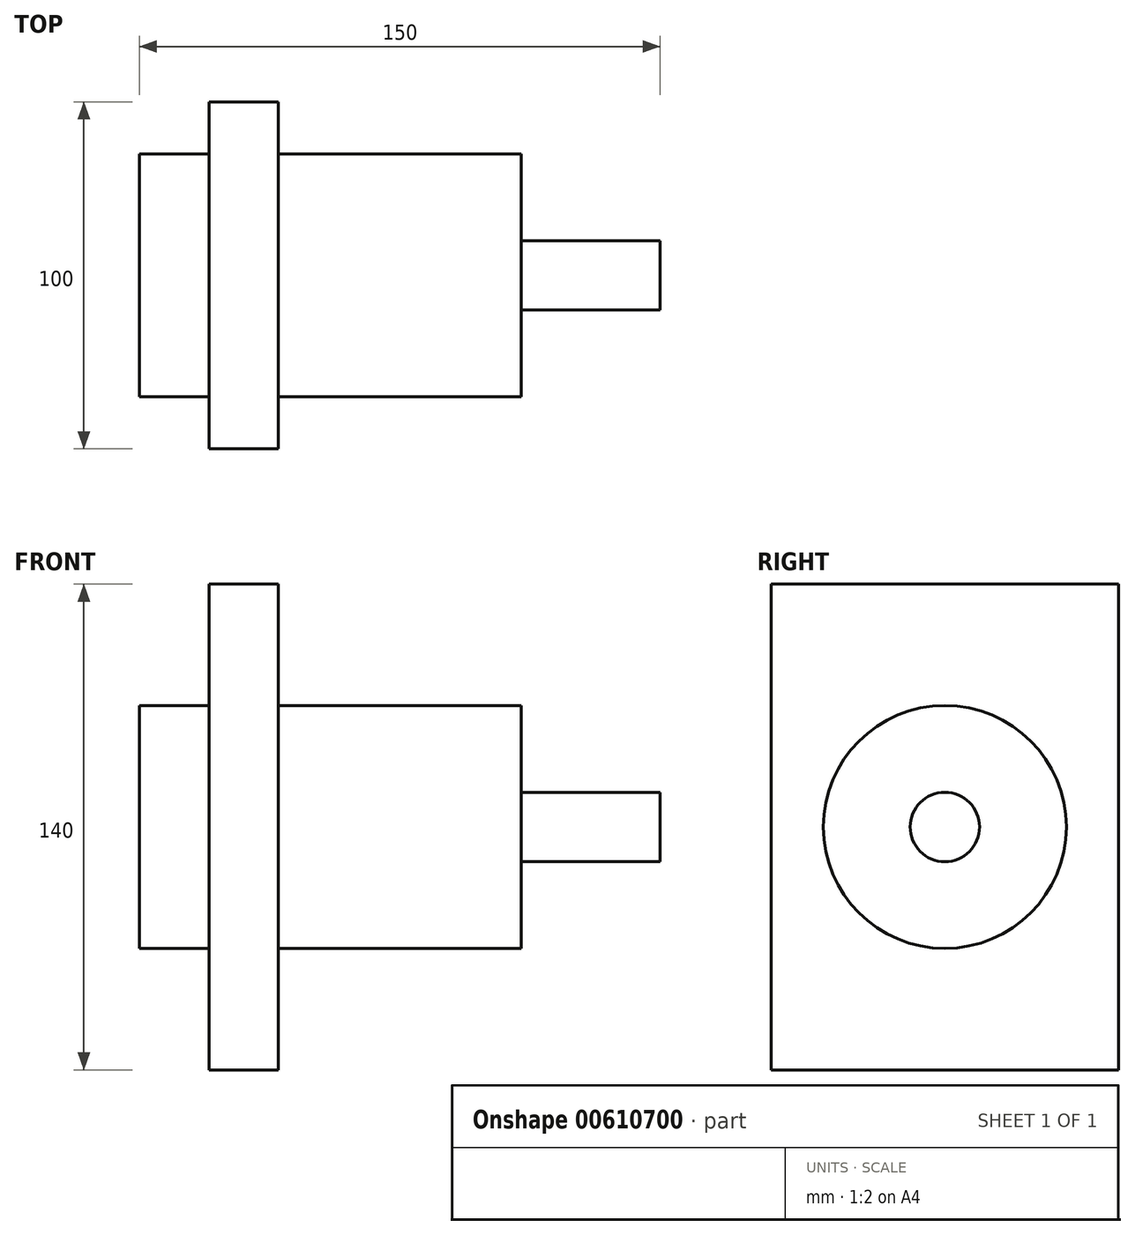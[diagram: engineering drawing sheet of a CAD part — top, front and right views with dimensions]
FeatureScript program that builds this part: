
annotation { "Feature Type Name" : "Feature", "Feature Type Description" : "" }
export const myFeature = defineFeature(function(context is Context, id is Id, definition is map)
    precondition{}
    {
        {
            var Q0;
            Q0=qCreatedBy(makeId("Right.planeOp"),FACE);
            var sketch = newSketch(context, id + "F0", { "sketchPlane" : qUnion([Q0])});
            skCircle(sketch, "E0", {"center": v(0, 0) * mm, "radius": 35 * mm});
            skSolve(sketch);
        }
        {
            var Q0;
            Q0 = qSketchRegion(id + "F0", true);
            extrude(context, id + "F1", {"entities" : qUnion([Q0]), "depth" : 70 * mm, "offsetDistance" : 25 * mm});
        }
        {
            var Q0;
            Q0=makeQuery(id+"F1.opExtrude","CAP_FACE",FACE,{"disambiguationData":[OSD([sQuery(id+"F0.wireOp",EDGE,"E0")])],"isStart":false});
            var sketch = newSketch(context, id + "F2", { "sketchPlane" : qUnion([Q0])});
            skCircle(sketch, "E1", {"center": v(0, 0) * mm, "radius": 10 * mm});
            skSolve(sketch);
        }
        {
            var Q0;
            Q0=makeQuery(id+"F2.imprint","IMPRINT",FACE,{"disambiguationData":[TD([[makeQuery(id+"F2.imprint","IMPRINT",EDGE,{"derivedFrom":sQuery(id+"F2.wireOp",EDGE,"E1")}),1.0]])]});
            extrude(context, id + "F3", {"entities" : qUnion([Q0]), "operationType" : NewBodyOperationType.ADD, "depth" : 40 * mm, "offsetDistance" : 25 * mm});
        }
        {
            var Q0;
            Q0=makeQuery(id+"F1.opExtrude","CAP_FACE",FACE,{"disambiguationData":[OSD([sQuery(id+"F0.wireOp",EDGE,"E0")])],"isStart":true});
            var sketch = newSketch(context, id + "F4", { "sketchPlane" : qUnion([Q0])});
            skLineSegment(sketch, "E2.bottom", {"start": v(-50, 70) * mm, "end": v(50, 70) * mm});
            skLineSegment(sketch, "E2.top", {"start": v(-50, -70) * mm, "end": v(50, -70) * mm});
            skLineSegment(sketch, "E2.left", {"start": v(-50, 70) * mm, "end": v(-50, -70) * mm});
            skLineSegment(sketch, "E2.right", {"start": v(50, 70) * mm, "end": v(50, -70) * mm});
            skSolve(sketch);
        }
        {
            var Q0;
            Q0=makeQuery(id+"F4.imprint","IMPRINT",FACE,{"disambiguationData":[TD([[makeQuery(id+"F4.imprint","IMPRINT",EDGE,{"derivedFrom":sQuery(id+"F4.wireOp",EDGE,"E2.bottom")}),-1.0]])]});
            var Q1;
            Q1=makeQuery(id+"F4.imprint","IMPRINT",FACE,{"disambiguationData":[TD([[makeQuery(id+"F4.imprint","IMPRINT",EDGE,{"derivedFrom":makeQuery(id+"F1.opExtrude","CAP_EDGE",EDGE,{"disambiguationData":[OSD([sQuery(id+"F0.wireOp",EDGE,"E0")])],"isStart":true})}),-1.0]])]});
            extrude(context, id + "F5", {"entities" : qUnion([Q0, Q1]), "operationType" : NewBodyOperationType.ADD, "depth" : 20 * mm, "offsetDistance" : 25 * mm});
        }
        {
            var Q0;
            Q0=makeQuery(id+"F5.opExtrude","CAP_FACE",FACE,{"disambiguationData":[OSD([sQuery(id+"F4.wireOp",EDGE,"E2.bottom"),sQuery(id+"F4.wireOp",EDGE,"E2.top"),sQuery(id+"F4.wireOp",EDGE,"E2.left"),sQuery(id+"F4.wireOp",EDGE,"E2.right")])],"isStart":false});
            var sketch = newSketch(context, id + "F6", { "sketchPlane" : qUnion([Q0])});
            skCircle(sketch, "E3", {"center": v(0, 0) * mm, "radius": 35 * mm});
            skSolve(sketch);
        }
        {
            var Q0;
            Q0=makeQuery(id+"F6.imprint","IMPRINT",FACE,{"disambiguationData":[TD([[makeQuery(id+"F6.imprint","IMPRINT",EDGE,{"derivedFrom":sQuery(id+"F6.wireOp",EDGE,"E3")}),1.0]])]});
            extrude(context, id + "F7", {"entities" : qUnion([Q0]), "operationType" : NewBodyOperationType.ADD, "depth" : 20 * mm, "offsetDistance" : 25 * mm});
        }
    });
